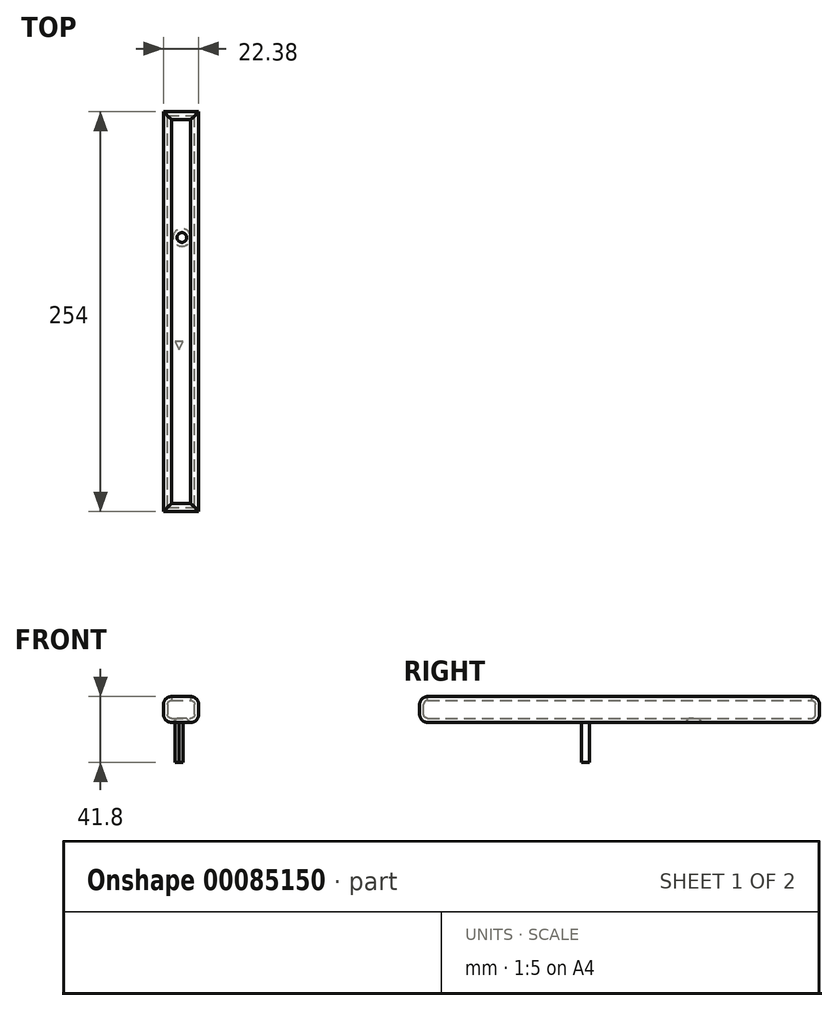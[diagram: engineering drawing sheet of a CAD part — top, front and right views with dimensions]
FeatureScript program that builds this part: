
annotation { "Feature Type Name" : "Feature", "Feature Type Description" : "" }
export const myFeature = defineFeature(function(context is Context, id is Id, definition is map)
    precondition{}
    {
        {
            var Q0;
            Q0=qCreatedBy(makeId("Front.planeOp"),FACE);
            var sketch = newSketch(context, id + "F0", { "sketchPlane" : qUnion([Q0])});
            skLineSegment(sketch, "E0", {"start": v(0, 0) * mm, "end": v(-22.38, 0) * mm});
            skLineSegment(sketch, "E1", {"start": v(-22.38, 0) * mm, "end": v(-22.38, -16.4) * mm});
            skLineSegment(sketch, "E2", {"start": v(-22.38, -16.4) * mm, "end": v(0, -16.4) * mm});
            skLineSegment(sketch, "E3", {"start": v(0, -16.4) * mm, "end": v(0, 0) * mm});
            skSolve(sketch);
        }
        {
            var Q0;
            Q0 = qSketchRegion(id + "F0", true);
            extrude(context, id + "F1", {"entities" : qUnion([Q0]), "depth" : 254 * mm});
        }
        {
            var Q0;
            Q0=makeQuery(id+"F1.opExtrude","SWEPT_FACE",FACE,{"disambiguationData":[OSD([sQuery(id+"F0.wireOp",EDGE,"E0")])]});
            var Q1;
            Q1=makeQuery(id+"F1.opExtrude","SWEPT_FACE",FACE,{"disambiguationData":[OSD([sQuery(id+"F0.wireOp",EDGE,"E2")])]});
            fillet(context, id + "F2", {"entities" : qUnion([Q0, Q1]), "radius" : 5.08 * mm, "tangentPropagation" : true, "allowEdgeOverflow" : false});
        }
        {
            var Q0;
            Q0=makeQuery(id+"F1.opExtrude","SWEPT_FACE",FACE,{"disambiguationData":[OSD([sQuery(id+"F0.wireOp",EDGE,"E0")])]});
            shell(context, id + "F3", {"entities" : qUnion([Q0]), "thickness" : 2.54 * mm});
        }
        {
            var Q0;
            Q0=makeQuery(id+"F1.opExtrude","SWEPT_FACE",FACE,{"disambiguationData":[OSD([sQuery(id+"F0.wireOp",EDGE,"E2")])]});
            var sketch = newSketch(context, id + "F4", { "sketchPlane" : qUnion([Q0])});
            skLineSegment(sketch, "E4", {"start": v(-12.44, 145.97) * mm, "end": v(-14.98, 145.97) * mm});
            skLineSegment(sketch, "E5", {"start": v(-14.98, 145.97) * mm, "end": v(-12.44, 151.05) * mm});
            skLineSegment(sketch, "E6", {"start": v(-12.44, 151.05) * mm, "end": v(-9.9, 145.97) * mm});
            skLineSegment(sketch, "E7", {"start": v(-9.9, 145.97) * mm, "end": v(-12.44, 145.97) * mm});
            skSolve(sketch);
        }
        {
            var Q0;
            Q0 = qSketchRegion(id + "F4", true);
            extrude(context, id + "F5", {"entities" : qUnion([Q0]), "operationType" : NewBodyOperationType.ADD, "depth" : 25.4 * mm});
        }
        {
            var Q0;
            Q0=makeQuery(id+"F1.opExtrude","SWEPT_FACE",FACE,{"disambiguationData":[OSD([sQuery(id+"F0.wireOp",EDGE,"E2")])]});
            var sketch = newSketch(context, id + "F6", { "sketchPlane" : qUnion([Q0])});
            skCircle(sketch, "E8", {"center": v(-10.68, 79.96) * mm, "radius": 4.56 * mm});
            skSolve(sketch);
        }
        {
            var Q0;
            Q0=sQuery(id+"F6.wireOp",VERTEX,"E8.center");
            var Q1;
            Q1=makeQuery(id+"F1.opExtrude","SWEPT_BODY",BODY,{"disambiguationData":[OSD([sQuery(id+"F0.wireOp",EDGE,"E0"),sQuery(id+"F0.wireOp",EDGE,"E1"),sQuery(id+"F0.wireOp",EDGE,"E2"),sQuery(id+"F0.wireOp",EDGE,"E3")])]});
            hole(context, id + "F7", {"style" : HoleStyle.C_SINK, "endStyle" : HoleEndStyle.THROUGH, "standardTappedOrClearance" : lookupTablePath({ "standard" : "ISO", "fit" : "Normal", "size" : "M5", "type" : "Clearance" }), "standardBlindInLast" : lookupTablePath({ "fit" : "Standard", "standard" : "ISO", "size" : "M5", "type" : "Clearance" }), "holeDiameter" : 5.5 * mm, "cSinkDiameter" : 11.2 * mm, "cSinkAngle" : 90 * degree, "locations" : qUnion([Q0]), "scope" : qUnion([Q1]), "isTappedThrough" : true});
        }
    });
